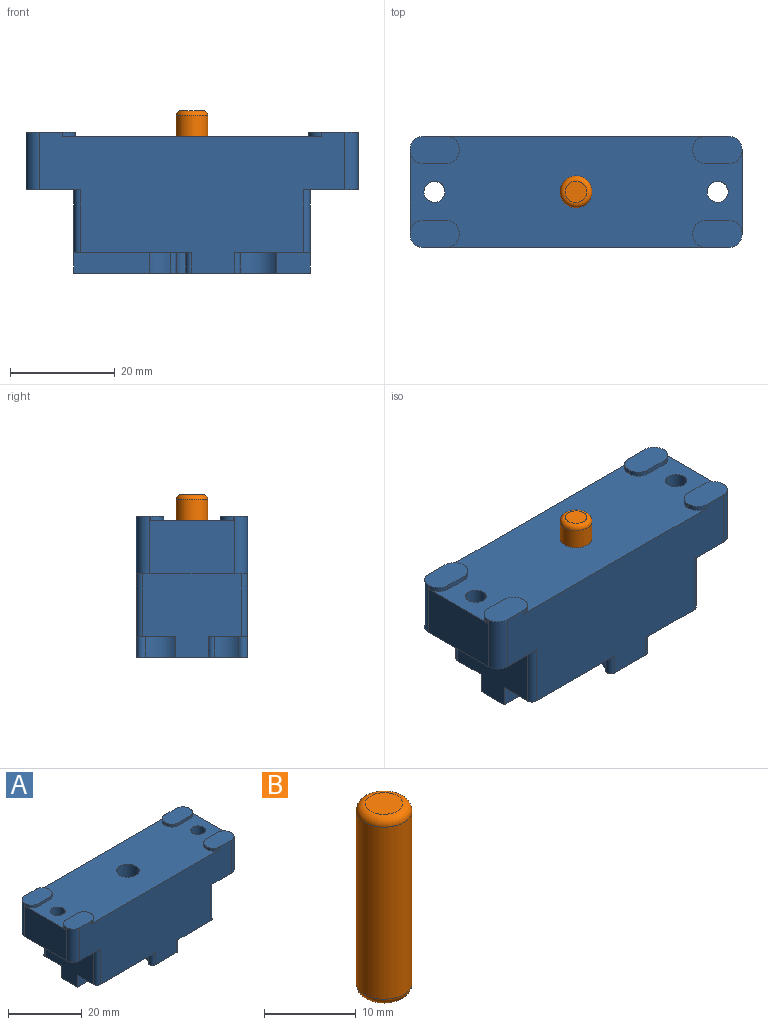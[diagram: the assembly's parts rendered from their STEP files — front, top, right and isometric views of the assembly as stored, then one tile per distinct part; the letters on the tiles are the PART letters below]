
ASSEMBLY  parts=2 mates=2
PART A: 68 faces, bbox 63.3x21.2x26.9 mm
  f0: plane 18.7x15.9mm, normal (1,0,0), area 247.3mm2, adj f1,f5,f6,f14,f50,f53,f58,f59
  f1: cylinder r=1.25mm len=11.9mm, axis (0,0,1), area 23.4mm2, adj f0,f13,f14,f59
  f2: cylinder r=1.25mm len=11.9mm, axis (0,0,1), area 23.4mm2, adj f3,f8,f13,f49
  f3: plane 18.7x15.9mm, normal (-1,0,0), area 247.3mm2, adj f2,f4,f7,f8,f46,f49,f54,f56
  f4: cylinder r=1.25mm len=11.9mm, axis (0,0,1), area 23.4mm2, adj f3,f8,f11,f56
  f5: cylinder r=1.25mm len=11.9mm, axis (0,0,1), area 23.4mm2, adj f0,f11,f14,f53
  f6: plane 23.69x13.7mm, normal (0,0,-1), area 171.1mm2, adj f0,f13,f45,f48,f50,f51,f57,f58
  f7: plane 23.69x13.7mm, normal (0,0,-1), area 171.1mm2, adj f3,f11,f45,f46,f47,f52,f54,f55
  f8: plane 21.2x10.4mm, normal (0,0,-1), area 179.4mm2, adj f2,f3,f4,f11,f12,f13,f16,f17
  f9: plane 63.3x21.2mm, normal (0,0,1), area 1108.2mm2, adj f10,f11,f12,f13,f19,f20,f21,f22
  f10: plane 16.2x11mm, normal (1,0,0), area 164mm2, adj f9,f14,f15,f18,f35,f36,f39,f42
  f11: plane 58.3x26.9mm, normal (0,1,0), area 1136mm2, adj f4,f5,f7,f8,f9,f14,f15,f16
  f12: plane 16.2x11mm, normal (-1,0,0), area 164mm2, adj f8,f9,f16,f17,f21,f24,f29,f30
  f13: plane 58.3x26.9mm, normal (0,-1,0), area 1136mm2, adj f1,f2,f6,f8,f9,f14,f17,f18
  f14: plane 21.2x10.4mm, normal (0,0,-1), area 179.4mm2, adj f0,f1,f5,f10,f11,f13,f15,f18
  f15: cylinder r=2.5mm len=11mm, axis (0,0,1), area 43.2mm2, adj f10,f11,f14,f36
  f16: cylinder r=2.5mm len=11mm, axis (0,0,-1), area 43.2mm2, adj f8,f11,f12,f24
  f17: cylinder r=2.5mm len=11mm, axis (0,0,1), area 43.2mm2, adj f8,f12,f13,f30
  f18: cylinder r=2.5mm len=11mm, axis (0,0,-1), area 43.2mm2, adj f10,f13,f14,f42
  f19: plane 0.9x0.2mm, normal (1,0,0), area 0.2mm2, adj f9,f20,f23,f24
  f20: cylinder r=2.5mm len=2.5mm, axis (0,0,-1), area 3.5mm2, adj f9,f11,f19,f24
  f21: cylinder r=2.5mm len=2.5mm, axis (0,0,-1), area 3.5mm2, adj f9,f12,f22,f24
  f22: plane 4.4x0.9mm, normal (0,-1,0), area 4mm2, adj f9,f21,f23,f24
  f23: cylinder r=2.5mm len=2.5mm, axis (0,0,-1), area 3.5mm2, adj f9,f19,f22,f24
  f24: plane 9.4x5.2mm, normal (0,0,1), area 43.5mm2, adj f11,f12,f16,f19,f20,f21,f22,f23
  f25: cylinder r=2.5mm len=2.5mm, axis (0,0,-1), area 3.5mm2, adj f9,f13,f26,f30
  f26: plane 0.9x0.2mm, normal (1,0,0), area 0.2mm2, adj f9,f25,f27,f30
  f27: cylinder r=2.5mm len=2.5mm, axis (0,0,-1), area 3.5mm2, adj f9,f26,f28,f30
  f28: plane 4.4x0.9mm, normal (0,1,0), area 4mm2, adj f9,f27,f29,f30
  f29: cylinder r=2.5mm len=2.5mm, axis (0,0,-1), area 3.5mm2, adj f9,f12,f28,f30
  f30: plane 9.4x5.2mm, normal (0,0,1), area 43.5mm2, adj f12,f13,f17,f25,f26,f27,f28,f29
  f31: cylinder r=2.5mm len=2.5mm, axis (0,0,-1), area 3.5mm2, adj f9,f11,f32,f36
  f32: plane 0.9x0.2mm, normal (-1,0,0), area 0.2mm2, adj f9,f31,f33,f36
  f33: cylinder r=2.5mm len=2.5mm, axis (0,0,-1), area 3.5mm2, adj f9,f32,f34,f36
  f34: plane 4.4x0.9mm, normal (0,-1,0), area 4mm2, adj f9,f33,f35,f36
  f35: cylinder r=2.5mm len=2.5mm, axis (0,0,-1), area 3.5mm2, adj f9,f10,f34,f36
  f36: plane 9.4x5.2mm, normal (0,0,1), area 43.5mm2, adj f10,f11,f15,f31,f32,f33,f34,f35
  f37: plane 0.9x0.2mm, normal (-1,0,0), area 0.2mm2, adj f9,f38,f41,f42
  f38: cylinder r=2.5mm len=2.5mm, axis (0,0,-1), area 3.5mm2, adj f9,f13,f37,f42
  f39: cylinder r=2.5mm len=2.5mm, axis (0,0,-1), area 3.5mm2, adj f9,f10,f40,f42
  f40: plane 4.4x0.9mm, normal (0,1,0), area 4mm2, adj f9,f39,f41,f42
  f41: cylinder r=2.5mm len=2.5mm, axis (0,0,-1), area 3.5mm2, adj f9,f37,f40,f42
  f42: plane 9.4x5.2mm, normal (0,0,1), area 43.5mm2, adj f10,f13,f18,f37,f38,f39,f40,f41
  f43: cylinder r=2mm len=10.1mm, axis (0,0,-1), area 126.9mm2, adj f9,f14
  f44: cylinder r=2mm len=10.1mm, axis (0,0,-1), area 126.9mm2, adj f8,f9
  f45: cylinder r=3.05mm len=26mm, axis (0,0,1), area 457mm2, adj f6,f7,f9,f49,f53,f62,f63,f66
  f46: plane 14.33x4mm, normal (0,-1,0), area 57.3mm2, adj f3,f7,f47,f49
  f47: cylinder r=4.65mm len=4.06mm, axis (0,0,-1), area 18.5mm2, adj f7,f46,f49,f67
  f48: cylinder r=4.65mm len=4.63mm, axis (0,0,-1), area 19.7mm2, adj f6,f49,f65,f66
  f49: plane 23.1x10.36mm, normal (0,0,-1), area 175.7mm2, adj f2,f3,f13,f45,f46,f47,f48,f65
  f50: plane 14.33x4mm, normal (0,1,0), area 57.3mm2, adj f0,f6,f51,f53
  f51: cylinder r=4.65mm len=4.06mm, axis (0,0,-1), area 18.5mm2, adj f6,f50,f53,f63
  f52: cylinder r=4.65mm len=4.63mm, axis (0,0,-1), area 19.7mm2, adj f7,f53,f61,f62
  f53: plane 23.1x10.36mm, normal (0,0,-1), area 175.7mm2, adj f0,f5,f11,f45,f50,f51,f52,f61
  f54: plane 6.33x4mm, normal (0,1,0), area 25.3mm2, adj f3,f7,f55,f56
  f55: cylinder r=4.65mm len=8.32mm, axis (0,0,-1), area 59.2mm2, adj f7,f54,f56,f64
  f56: plane 14.65x9.3mm, normal (0,0,-1), area 114.9mm2, adj f3,f4,f11,f54,f55,f64
  f57: cylinder r=4.65mm len=8.32mm, axis (0,0,-1), area 59.2mm2, adj f6,f58,f59,f60
  f58: plane 6.33x4mm, normal (0,-1,0), area 25.3mm2, adj f0,f6,f57,f59
  f59: plane 14.65x9.3mm, normal (0,0,-1), area 114.9mm2, adj f0,f1,f13,f57,f58,f60
  f60: cylinder r=1mm len=4mm, axis (0,0,-1), area 9.1mm2, adj f6,f13,f57,f59
  f61: cylinder r=1mm len=4mm, axis (0,0,-1), area 9.1mm2, adj f7,f11,f52,f53
  f62: cylinder r=1mm len=4mm, axis (0,0,-1), area 6.9mm2, adj f7,f45,f52,f53
  f63: cylinder r=1mm len=4mm, axis (0,0,-1), area 6.9mm2, adj f6,f45,f51,f53
  f64: cylinder r=1mm len=4mm, axis (0,0,-1), area 9.1mm2, adj f7,f11,f55,f56
  f65: cylinder r=1mm len=4mm, axis (0,0,-1), area 9.1mm2, adj f6,f13,f48,f49
  f66: cylinder r=1mm len=4mm, axis (0,0,-1), area 6.9mm2, adj f6,f45,f48,f49
  f67: cylinder r=1mm len=4mm, axis (0,0,-1), area 6.9mm2, adj f7,f45,f47,f49
PART B: 5 faces, bbox 6.6x6.6x25 mm
  f0: cylinder r=3.05mm len=23mm, axis (0,0,-1), area 440.8mm2, adj f3,f4
  f1: plane 4.1x4.1mm, normal (0,0,1), area 13.2mm2, adj f4
  f2: plane 4.1x4.1mm, normal (0,0,-1), area 13.2mm2, adj f3
  f3: torus R=2.05mm, axis (0,0,1), area 26.5mm2, adj f0,f2
  f4: torus R=2.05mm, axis (0,0,1), area 26.5mm2, adj f0,f1
PLACE A t=(5.05,-4.57,2.27)mm fixed
PLACE B rot(axis=(0,0,1),0deg) t=(5.05,-4.57,-7.63)mm
MATE planar B.f0 <-> A.f45  axis (0,0,1) through (5.05,-4.57,17.37)mm
MATE cylindrical B.f0 <-> A.f45  axis (0,0,-1) through (5.05,-4.57,4.87)mm
